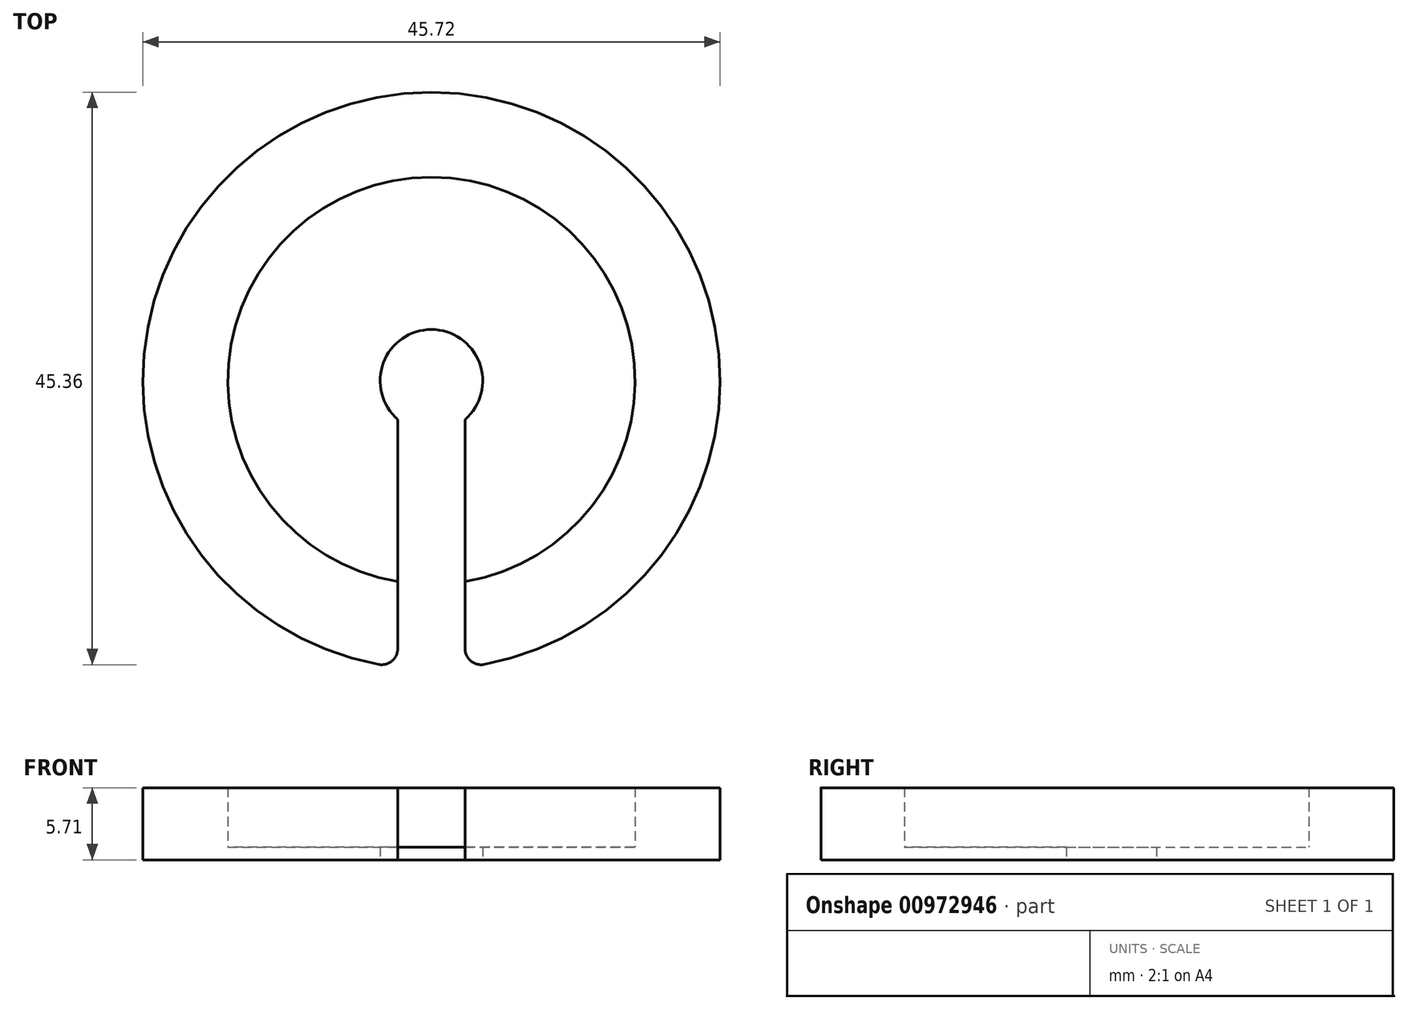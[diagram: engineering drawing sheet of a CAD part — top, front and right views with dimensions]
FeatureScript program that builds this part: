
annotation { "Feature Type Name" : "Feature", "Feature Type Description" : "" }
export const myFeature = defineFeature(function(context is Context, id is Id, definition is map)
    precondition{}
    {
        {
            var Q0;
            Q0=qCreatedBy(makeId("Top.planeOp"),FACE);
            var sketch = newSketch(context, id + "F0", { "sketchPlane" : qUnion([Q0])});
            skArc(sketch, "E0", {"start": v(2.67, -3.07) * mm, "mid": v(0, 4.06) * mm, "end": v(-2.67, -3.07) * mm});
            skArc(sketch, "E1.0", {"start": v(2.67, -22.7) * mm, "mid": v(0, 22.86) * mm, "end": v(-2.67, -22.7) * mm});
            skLineSegment(sketch, "E2", {"start": v(-2.67, -22.7) * mm, "end": v(-2.67, -3.07) * mm});
            skLineSegment(sketch, "E3", {"start": v(2.67, -3.07) * mm, "end": v(2.67, -22.7) * mm});
            skSolve(sketch);
        }
        {
            var Q0;
            Q0=makeQuery(id+"F0.imprint","IMPRINT",FACE,{"disambiguationData":[TD([[makeQuery(id+"F0.imprint","IMPRINT",EDGE,{"derivedFrom":sQuery(id+"F0.wireOp",EDGE,"E0")}),-1.0]])]});
            extrude(context, id + "F1", {"entities" : qUnion([Q0]), "depth" : 1.02 * mm});
        }
        {
            var Q0;
            Q0=makeQuery(id+"F1.opExtrude","CAP_FACE",FACE,{"disambiguationData":[OSD([sQuery(id+"F0.wireOp",EDGE,"E0"),sQuery(id+"F0.wireOp",EDGE,"E1.0"),sQuery(id+"F0.wireOp",EDGE,"E2"),sQuery(id+"F0.wireOp",EDGE,"E3")])],"isStart":false});
            var sketch = newSketch(context, id + "F2", { "sketchPlane" : qUnion([Q0])});
            skCircle(sketch, "E4", {"center": v(0, 0) * mm, "radius": 22.86 * mm});
            skCircle(sketch, "E5.0", {"center": v(0, 0) * mm, "radius": 16.13 * mm});
            skSolve(sketch);
        }
        {
            var Q0;
            {var subQ0=sQuery(id+"F2.wireOp",EDGE,"E4");var subQ1=makeQuery(id+"F1.opExtrude","CAP_EDGE",EDGE,{"disambiguationData":[OSD([sQuery(id+"F0.wireOp",EDGE,"E3")])],"isStart":false});var subQ2=makeQuery(id+"F2.imprint","INTERSECT",VERTEX,{"derivedFrom":[subQ1,subQ0]});Q0=makeQuery(id+"F2.imprint","IMPRINT",FACE,{"disambiguationData":[TD([[makeQuery(id+"F2.imprint","IMPRINT",EDGE,{"disambiguationData":[TD([[subQ2,-1.0]])],"derivedFrom":subQ0}),1.0]])]});}
            extrude(context, id + "F3", {"entities" : qUnion([Q0]), "operationType" : NewBodyOperationType.ADD, "depth" : 4.7 * mm});
        }
        {
            var Q0;
            {var subQ0=sQuery(id+"F0.wireOp",EDGE,"E2");Q0=makeQuery(id+"F3.boolean.opBoolean","MERGE",EDGE,{"derivedFrom":[makeQuery(id+"F1.opExtrude","SWEPT_EDGE",EDGE,{"disambiguationData":[OSD([sQuery(id+"F0.wireOp",EDGE,"E1.0"),subQ0])]}),makeQuery(id+"F3.opExtrude","SWEPT_EDGE",EDGE,{"disambiguationData":[OSD([subQ0,sQuery(id+"F2.wireOp",EDGE,"E4")])]})]});}
            var Q1;
            {var subQ0=sQuery(id+"F0.wireOp",EDGE,"E3");Q1=makeQuery(id+"F3.boolean.opBoolean","MERGE",EDGE,{"derivedFrom":[makeQuery(id+"F1.opExtrude","SWEPT_EDGE",EDGE,{"disambiguationData":[OSD([sQuery(id+"F0.wireOp",EDGE,"E1.0"),subQ0])]}),makeQuery(id+"F3.opExtrude","SWEPT_EDGE",EDGE,{"disambiguationData":[OSD([subQ0,sQuery(id+"F2.wireOp",EDGE,"E4")])]})]});}
            fillet(context, id + "F4", {"entities" : qUnion([Q0, Q1]), "radius" : 1.27 * mm, "tangentPropagation" : true, "allowEdgeOverflow" : false});
        }
    });
